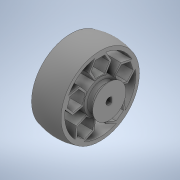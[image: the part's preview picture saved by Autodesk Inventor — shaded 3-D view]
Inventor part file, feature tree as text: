
AUTODESK INVENTOR PART (.ipt)
format: ipt  version: 2020 (Build 240168000, 168)  size: 373,760 bytes
history: native  units: in
note: dims shown in document units (in); Inventor stores cm internally (conversion verified against a paired STEP export)
features: sketch x4, extrude x2, revolve x2, projected_geometry x1
ambient origin geometry x8: Origin, YZ Plane, XZ Plane, XY Plane, X Axis, Y Axis, Z Axis, Center Point
bodies: Solid1 (feature_tree)
feature tree (9):
  extrude  "Extrusion1"  Depth=0.0394in
  sketch  "Sketch3"  dims[d6=0.5748in d7=0.1575in]
  revolve  "Revolution1"  [1 undecoded]
  extrude  "Extrusion2"  Depth=0.1575in
  revolve  "Revolution2"  [1 undecoded]
  sketch  "Sketch1"  dims[d0=0.1181in d1=0.0394in]
  sketch  "Sketch2"  dims[d3=1.3583in d4=0.1181in]
  projected_geometry  "Projected Loop1"
  sketch  "Sketch4"  dims[d8=0.0in d9=1.3583in d10=0.063in d11=0.0315in d16=0.5118in d17=0.0in d19=360.0deg d20=0.0787in d24=0.0394in d25=90.0deg d26=45.0deg d28=0.0079in d29=1.9685in d31=360.0deg]
note: 2 required parameter values undecoded (feature->parameter linkage not recoverable at this tier; creation-order binding heuristic only, values carry confidence <= 0.55)
